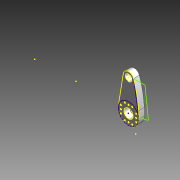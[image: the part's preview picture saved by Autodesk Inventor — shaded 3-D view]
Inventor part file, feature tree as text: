
AUTODESK INVENTOR PART (.ipt)
format: ipt  version: 2014 SP1 (Build 180222100, 222)  size: 217,600 bytes
history: native  units: in
note: dims shown in document units (in); Inventor stores cm internally (conversion verified against a paired STEP export)
features: extrude x5, sketch x5, fillet x2, other x1, move_body x1, imported_body x1
ambient origin geometry x8: Origin, YZ Plane, XZ Plane, XY Plane, X Axis, Y Axis, Z Axis, Center Point
bodies: Solid1 (feature_tree)
feature tree (15):
  other  "Component7.ipt1"
  move_body  "Move Body1"
  extrude  "Extrusion1"  Depth=0.25in
  extrude  "Extrusion2"  Depth=0.1969in TaperAngle=0.0deg
  extrude  "Extrusion3"  Depth=0.1969in TaperAngle=0.0deg
  extrude  "Extrusion4"  Depth=0.1575in
  extrude  "Extrusion5"  Depth=0.0787in
  fillet  "Fillet1"  Radius=0.0394in
  fillet  "Fillet2"  [1 undecoded]
  imported_body  "Base1"
  sketch  "Sketch1"  dims[d0=180.0deg d1=0.25in]
  sketch  "Sketch2"  dims[d2=0.4075in d3=0.1969in d4=0.0in]
  sketch  "Sketch3"  dims[d5=0.1969in d6=0.0in d10=0.1969in d11=0.0in]
  sketch  "Sketch4"  dims[d12=0.1969in d13=0.0in d14=0.1575in]
  sketch  "Sketch5"  dims[d15=0.1969in d16=0.0in d17=0.0787in d18=0.0394in]
note: 1 required parameter value undecoded (feature->parameter linkage not recoverable at this tier; creation-order binding heuristic only, values carry confidence <= 0.55)
